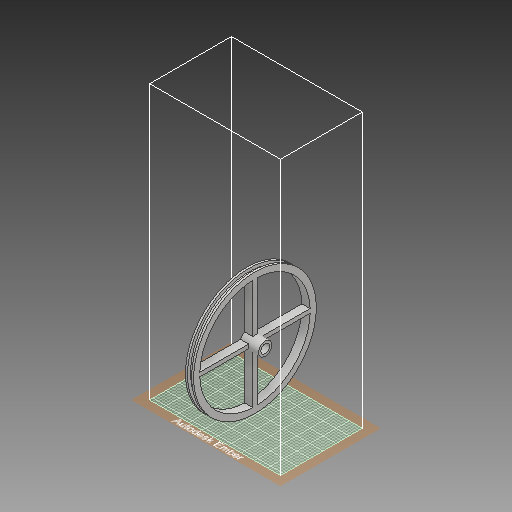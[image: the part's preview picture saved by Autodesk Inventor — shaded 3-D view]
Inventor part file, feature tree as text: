
AUTODESK INVENTOR PART (.ipt)
format: ipt  version: 2018 (Build 220112000, 112)  size: 388,608 bytes
history: native  units: mm
features: extrude x10, sketch x10, fillet x2, pattern_circular x1
ambient origin geometry x8: Origin, YZ Plane, XZ Plane, XY Plane, X Axis, Y Axis, Z Axis, Center Point
bodies: Solid1 (feature_tree)
feature tree (23):
  extrude  "Extrusion1"  Depth=2.0mm TaperAngle=0.0deg
  extrude  "Extrusion2"  Depth=1.0mm TaperAngle=0.0deg
  extrude  "Extrusion3"  Depth=1.0mm TaperAngle=0.0deg
  extrude  "Extrusion4"  Depth=10.0mm TaperAngle=0.0deg
  extrude  "Extrusion5"  Depth=6.5mm
  extrude  "Extrusion6"  Depth=1.0mm
  pattern_circular  "Circular Pattern1"  Count=4 Angle=360.0deg
  extrude  "Extrusion7"  Depth=5.0mm
  extrude  "Extrusion8"  Depth=2.0mm TaperAngle=0.0deg
  extrude  "Extrusion9"  Depth=4.5mm
  extrude  "Extrusion10"  Depth=2.0mm
  fillet  "Fillet1"  Radius=5.0mm
  fillet  "Fillet2"  Radius=4.5mm
  sketch  "Sketch1"  dims[d0=57.0mm d1=2.0mm d2=0.0mm]
  sketch  "Sketch2"  dims[d3=60.0mm d4=1.0mm d5=0.0mm]
  sketch  "Sketch3"  dims[d6=60.0mm d7=1.0mm d8=0.0mm]
  sketch  "Sketch4"  dims[d9=54.0mm d10=10.0mm d11=0.0mm]
  sketch  "Sketch5"  dims[d12=4.25mm d13=6.5mm]
  sketch  "Sketch6"  dims[d14=4.0mm d15=0.0mm d16=1.0mm]
  sketch  "Sketch7"  dims[d17=2.0mm]
  sketch  "Sketch8"  dims[d18=4.0mm d19=0.0mm d20=40.0mm d21=360.0deg]
  sketch  "Sketch9"  dims[d23=5.0mm d24=0.0mm d25=9.0mm]
  sketch  "Sketch10"  dims[d26=4.25mm d27=9.0mm d28=0.0mm d29=4.5mm d30=7.0mm d31=5.0mm d32=0.0mm d33=4.5mm d34=5000.0mm d35=0.0mm d36=2.0mm d37=2.0mm]
